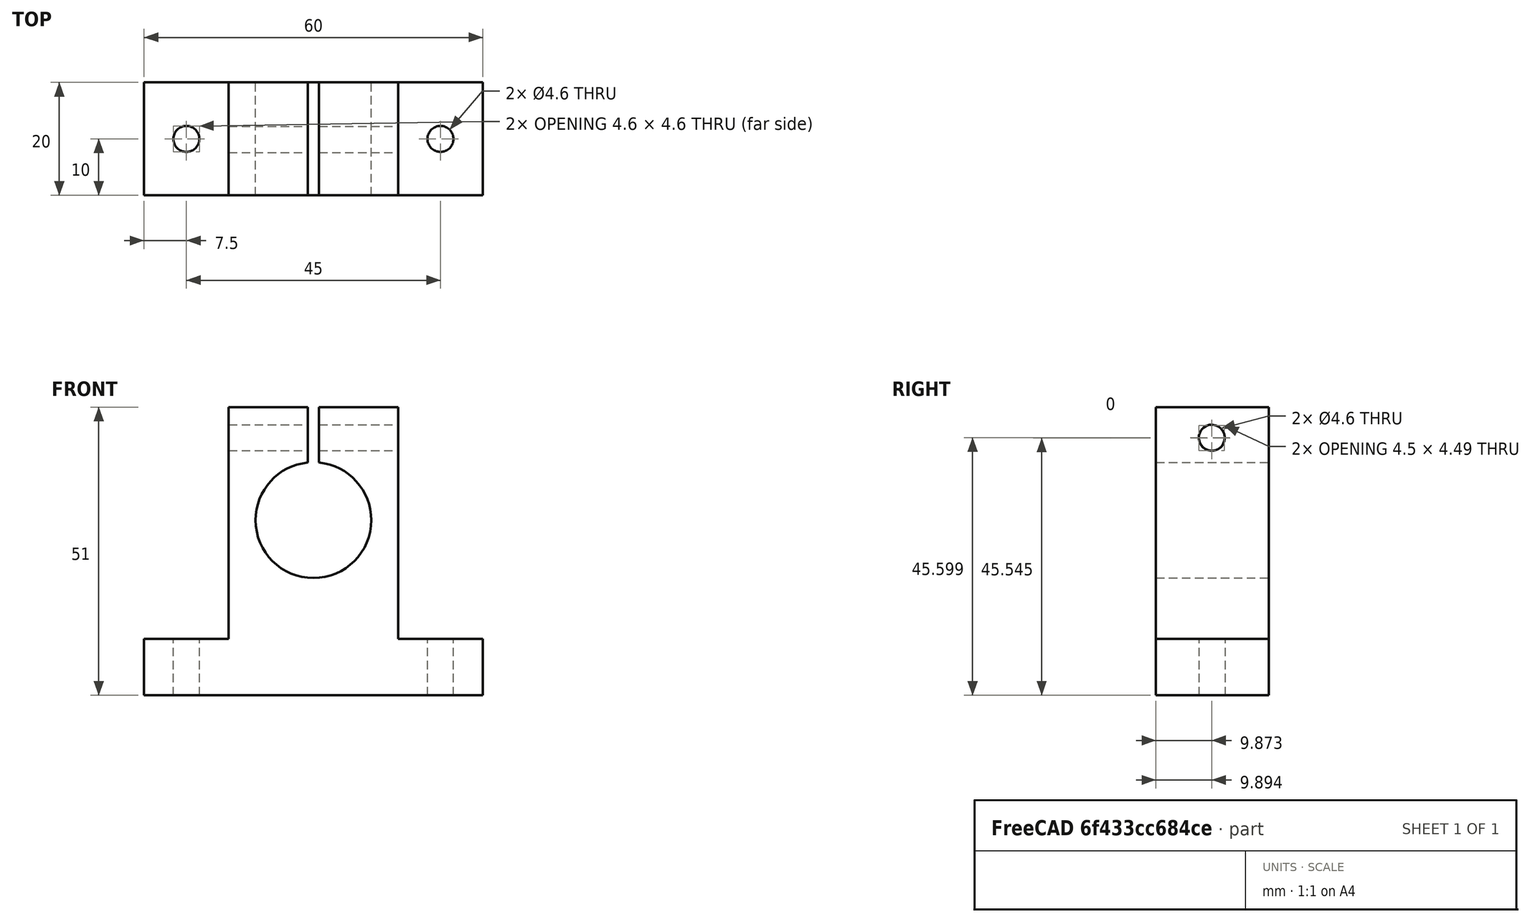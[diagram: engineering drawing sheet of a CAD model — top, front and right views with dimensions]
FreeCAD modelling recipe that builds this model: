
FCSTD DOCUMENT
Label: sk20
objects: Part::Cut×5, Part::Cylinder×4, Part::Box×3, Part::Fuse×1
note: 13 computed .brp shape members not serialized (recipe doc carries the construction recipe); baked Part::Feature solids carry a one-line shape summary decoded from their .brp

FEATURE [Part::Box] Box
  Height = 10
  Length = 60
  Width = 20
FEATURE [Part::Box] Box001
  Height = 41
  Length = 30
  Placement = pos=(15,0,10) rot=(0,0,1;0rad)
  Width = 20
FEATURE [Part::Cylinder] Cylinder
  Angle = 360
  Height = 25
  Placement = pos=(30,-3.23131,31) rot=(-1,0,0;1.5708rad)
  Radius = 10.25
FEATURE [Part::Cut] Cut
  Base = -> Box001
  Tool = -> Cylinder
FEATURE [Part::Fuse] Fusion
  Base = -> Box
  Tool = -> Cut
FEATURE [Part::Cylinder] Cylinder001
  Angle = 360
  Height = 13
  Placement = pos=(7.5,10,-2) rot=(0,0,1;0rad)
  Radius = 2.3
FEATURE [Part::Cut] Cut001
  Base = -> Fusion
  Tool = -> Cylinder001
FEATURE [Part::Cylinder] Cylinder002
  Angle = 360
  Height = 13
  Placement = pos=(52.5,10,-2) rot=(0,0,1;0rad)
  Radius = 2.3
FEATURE [Part::Cut] Cut002
  Base = -> Cut001
  Tool = -> Cylinder002
FEATURE [Part::Cylinder] Cylinder003
  Angle = 360
  Height = 33
  Placement = pos=(13.1208,9.89392,45.5993) rot=(0,1,0;1.5708rad)
  Radius = 2.3
FEATURE [Part::Cut] Cut003
  Base = -> Cut002
  Tool = -> Cylinder003
FEATURE [Part::Box] Box002
  Height = 15
  Length = 2
  Placement = pos=(29,-2.73,37.37) rot=(0,0,1;0rad)
  Width = 25
FEATURE [Part::Cut] Cut004
  Base = -> Cut003
  Tool = -> Box002
